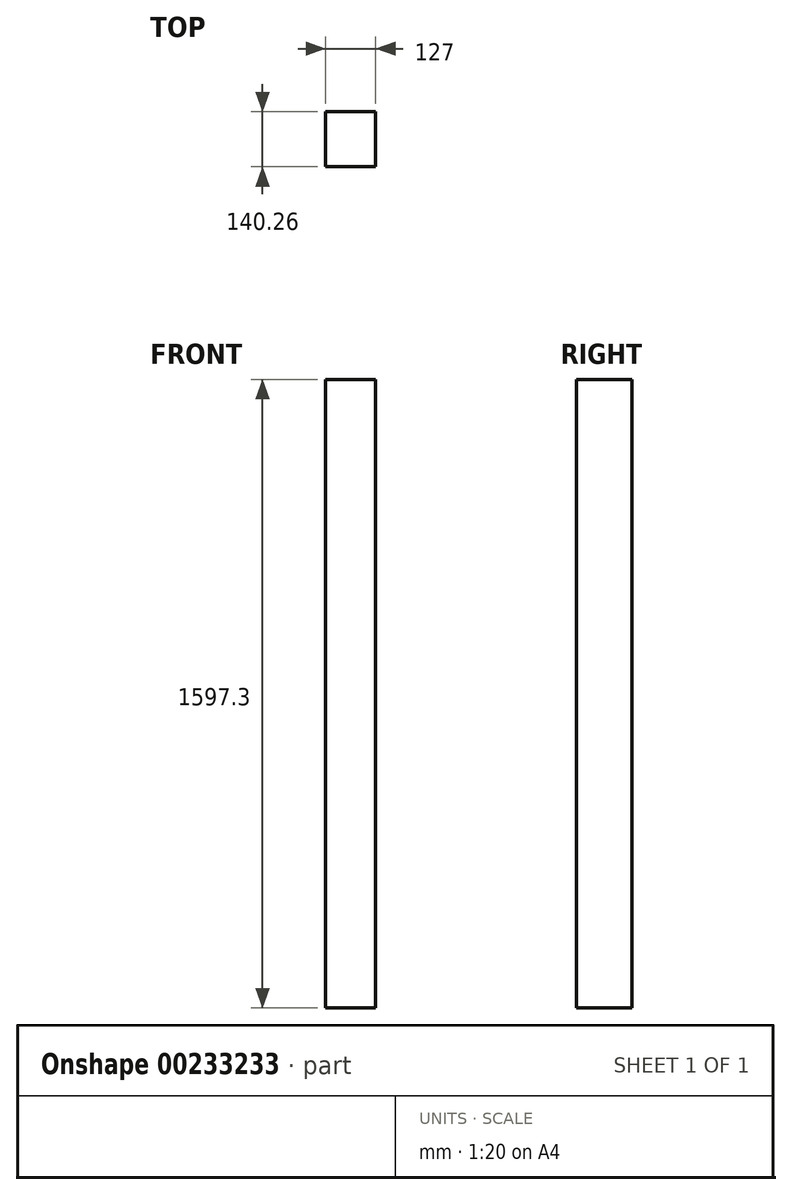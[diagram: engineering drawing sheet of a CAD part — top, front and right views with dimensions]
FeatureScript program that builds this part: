
annotation { "Feature Type Name" : "Feature", "Feature Type Description" : "" }
export const myFeature = defineFeature(function(context is Context, id is Id, definition is map)
    precondition{}
    {
        {
            var Q0;
            Q0=qCreatedBy(makeId("Right.planeOp"),FACE);
            var sketch = newSketch(context, id + "F0", { "sketchPlane" : qUnion([Q0])});
            skLineSegment(sketch, "E0.bottom", {"start": v(-72.3, -138.24) * mm, "end": v(67.96, -138.24) * mm});
            skLineSegment(sketch, "E0.top", {"start": v(-72.3, 1459.06) * mm, "end": v(67.96, 1459.06) * mm});
            skLineSegment(sketch, "E0.left", {"start": v(-72.3, -138.24) * mm, "end": v(-72.3, 1459.06) * mm});
            skLineSegment(sketch, "E0.right", {"start": v(67.96, -138.24) * mm, "end": v(67.96, 1459.06) * mm});
            skSolve(sketch);
        }
        {
            var Q0;
            Q0=makeQuery(id+"F0.imprint","IMPRINT",FACE,{"disambiguationData":[TD([[makeQuery(id+"F0.imprint","IMPRINT",EDGE,{"derivedFrom":sQuery(id+"F0.wireOp",EDGE,"E0.bottom")}),1.0]])]});
            extrude(context, id + "F1", {"entities" : qUnion([Q0]), "depth" : 127 * mm});
        }
    });
